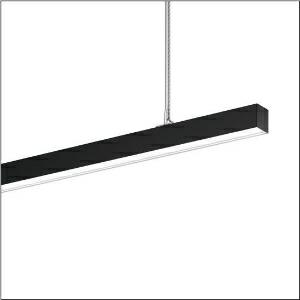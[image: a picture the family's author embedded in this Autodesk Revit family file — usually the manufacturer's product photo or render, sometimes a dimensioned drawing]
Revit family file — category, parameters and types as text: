
# Revit family: silica_21_51mx30tbt5b
name_source: partatom
category: Lighting Fixtures
units: mm (PartAtom-declared; Revit-internal decimal feet)

## family parameters
Cut with Voids When Loaded = No
Host = Face
Light Source = No
Part Type = Normal
Room Calculation Point = No
Round Connector Dimension = Use Diameter
Shared = No

## types (1)
- --- (1 x LED, 5150 lm, 42.2 W, 6500K)
    Apparent Load = 42 VA
    CIE Flux Codes = 47 79 96 58 100
    Color Rendering = 80
    Color Temperature = 6500K
    Default Elevation = 1800 mm
    Description = Silica 21, office luminaire, primary optical cover: cover, of PMMA, opal, light emission: direct/indirect distribution, primary light characteristic: symmetric, installation type: suspended mounting, LED, rated luminous flux: 5.150lm, luminous efficacy: 116lm/W, light colour: 8tw, colour temperature: 2700..6500K, control gear: DALI DT8, with terminal, 3+2-pole, max. 2.5mm², mains connection: 220..240V, AC, 50/60Hz, rated input power: 44.3W, luminaire housing, of aluminium, matt jet black (RAL 9005), length: 1.504mm, width: 53mm, height: 53mm, protection rating (complete): IP20, insulation class (complete): insulation class I (protective earthing), certification: CE, permissible operating ambient temperature: 0..+35°C, standard: EN 50419, packaging unit: 1 piece
    Height = 53 mm
    Lamp = 1 x LED
    Lamp Light Flux = 5150 lm
    Lamp Power = 42.2 W
    Lamp count = 1
    Length = 1504 mm
    Luminous efficacy = 122 lm/W
    Manufacturer = Siteco
    ModVariant = No
    Model = 51MX30TBT5B
    Mounting Place = Ceiling
    Mounting Type = Pendant
    Number of Poles = 1
    OnlyDefault = Yes
    Power Factor = 1
    Product Name = Silica 21
    Product group = office luminaire | ceiling pendant
    ProductGroupID = 903
    Protection Class = Protection class I
    Protection Degree = IP 20
    RLX_Detail_Level = 1
    RLX_Emergency_Light_Flux = 0 lm
    RLX_Emergency_Type = 0
    RLX_Emergency_Type_DB = No
    RlxData = <blob elided: 22869 chars, md5=5c1f9b12>
    Socket = socket
    Standby Power = 0 W
    System Light Flux = 5150 lm
    System Power = 42 W
    Type Comments = individual setting
    Type Image = l_1335856.jpg
    URL = http://relux.com
    VarID = @adj_139127
    Voltage = 0 V
    Weight = 0.00 kg
    Width = 53 mm

## geometry (parser evidence)
native form markers: Blend x4, Sweep x13
no freeform markers — native parametric forms only
